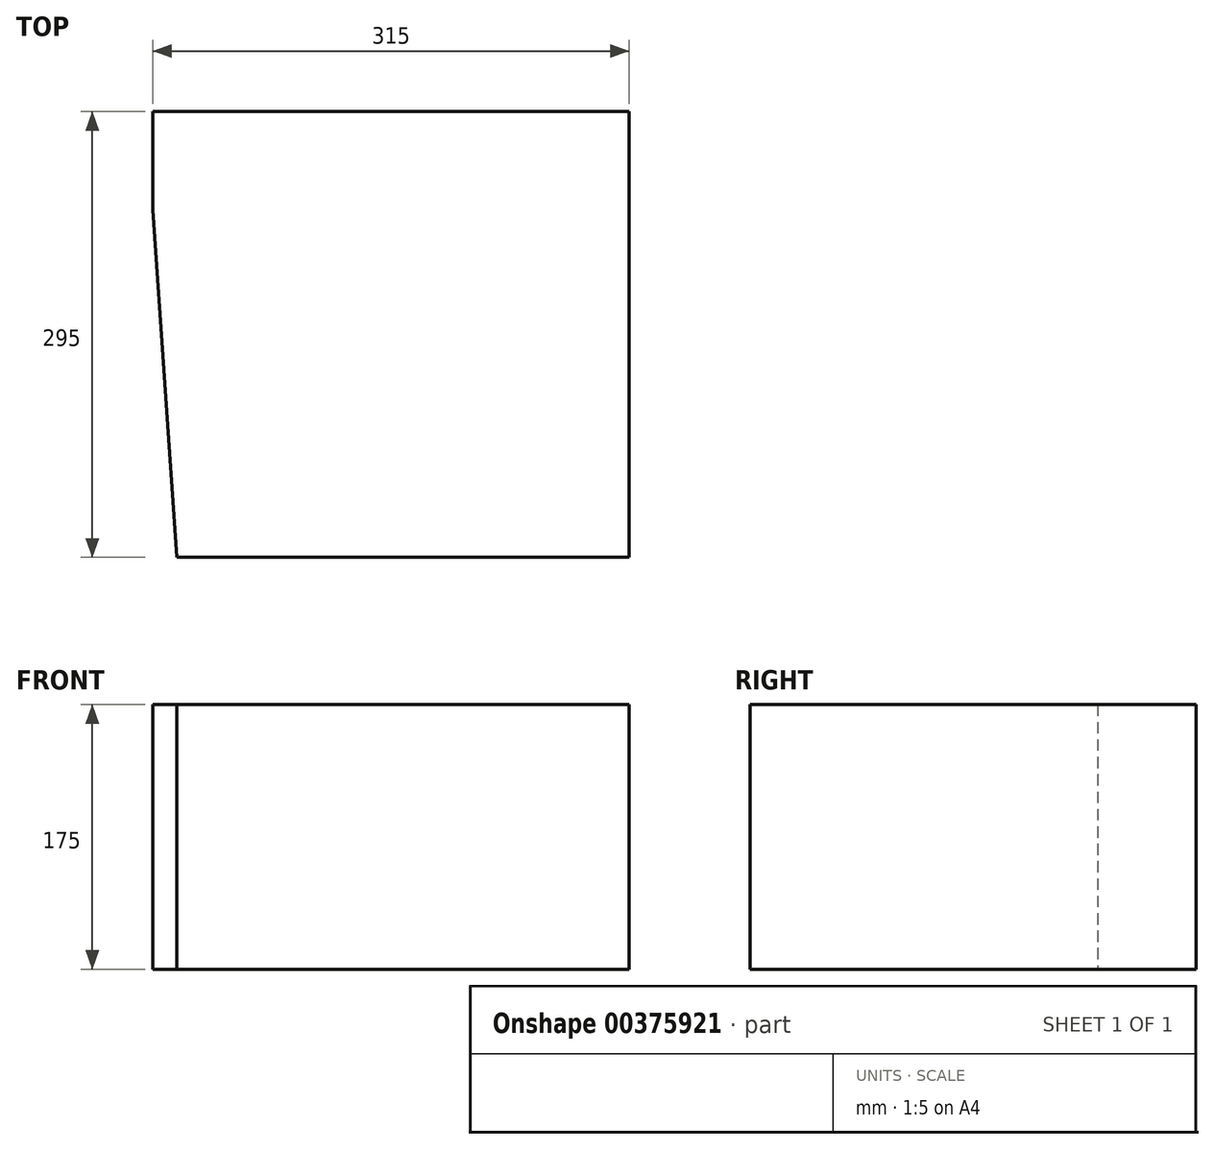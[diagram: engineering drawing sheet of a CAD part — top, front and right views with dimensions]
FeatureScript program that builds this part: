
annotation { "Feature Type Name" : "Feature", "Feature Type Description" : "" }
export const myFeature = defineFeature(function(context is Context, id is Id, definition is map)
    precondition{}
    {
        {
            var Q0;
            Q0=qCreatedBy(makeId("Top.planeOp"),FACE);
            var sketch = newSketch(context, id + "F0", { "sketchPlane" : qUnion([Q0])});
            skLineSegment(sketch, "E0.bottom", {"start": v(-105, 165.77) * mm, "end": v(210, 165.77) * mm});
            skLineSegment(sketch, "E0.top", {"start": v(-84, -129.23) * mm, "end": v(210, -129.23) * mm});
            skLineSegment(sketch, "E0.right", {"start": v(210, 165.77) * mm, "end": v(210, -129.23) * mm});
            skLineSegment(sketch, "E1", {"start": v(0, 212.18) * mm, "end": v(0, -211.28) * mm, "construction": true});
            skLineSegment(sketch, "E2.0", {"start": v(-109.5, 165.42) * mm, "end": v(-95.27, -39.24) * mm, "construction": true});
            skLineSegment(sketch, "E3", {"start": v(-172.54, 100.77) * mm, "end": v(-53.57, 100.77) * mm, "construction": true});
            skLineSegment(sketch, "E4", {"start": v(-157.1, -39.23) * mm, "end": v(-49.36, -39.23) * mm, "construction": true});
            skLineSegment(sketch, "E5", {"start": v(-105, 100.77) * mm, "end": v(-105, 165.77) * mm});
            skLineSegment(sketch, "E6", {"start": v(-105, 100.77) * mm, "end": v(-95.27, -39.24) * mm});
            skLineSegment(sketch, "E7", {"start": v(-95.27, -39.24) * mm, "end": v(-89.01, -129.23) * mm});
            skLineSegment(sketch, "E8", {"start": v(-89.01, -129.23) * mm, "end": v(-84, -129.23) * mm});
            skSolve(sketch);
        }
        {
            var Q0;
            Q0=qSketchRegion(id+"F0",true);
            extrude(context, id + "F1", {"entities" : qUnion([Q0]), "depth" : 175 * mm});
        }
        {
            var Q0;
            Q0=makeQuery(id+"F0.imprint","IMPRINT",FACE,{"disambiguationData":[TD([[makeQuery(id+"F0.imprint","IMPRINT",EDGE,{"derivedFrom":sQuery(id+"F0.wireOp",EDGE,"E0.bottom")}),-1.0]])]});
            cPlane(context, id + "F2", {"entities" : qUnion([Q0]), "cplaneType" : CPlaneType.OFFSET, "offset" : 114 * mm, "width" : 150 * mm, "height" : 150 * mm});
        }
    });
